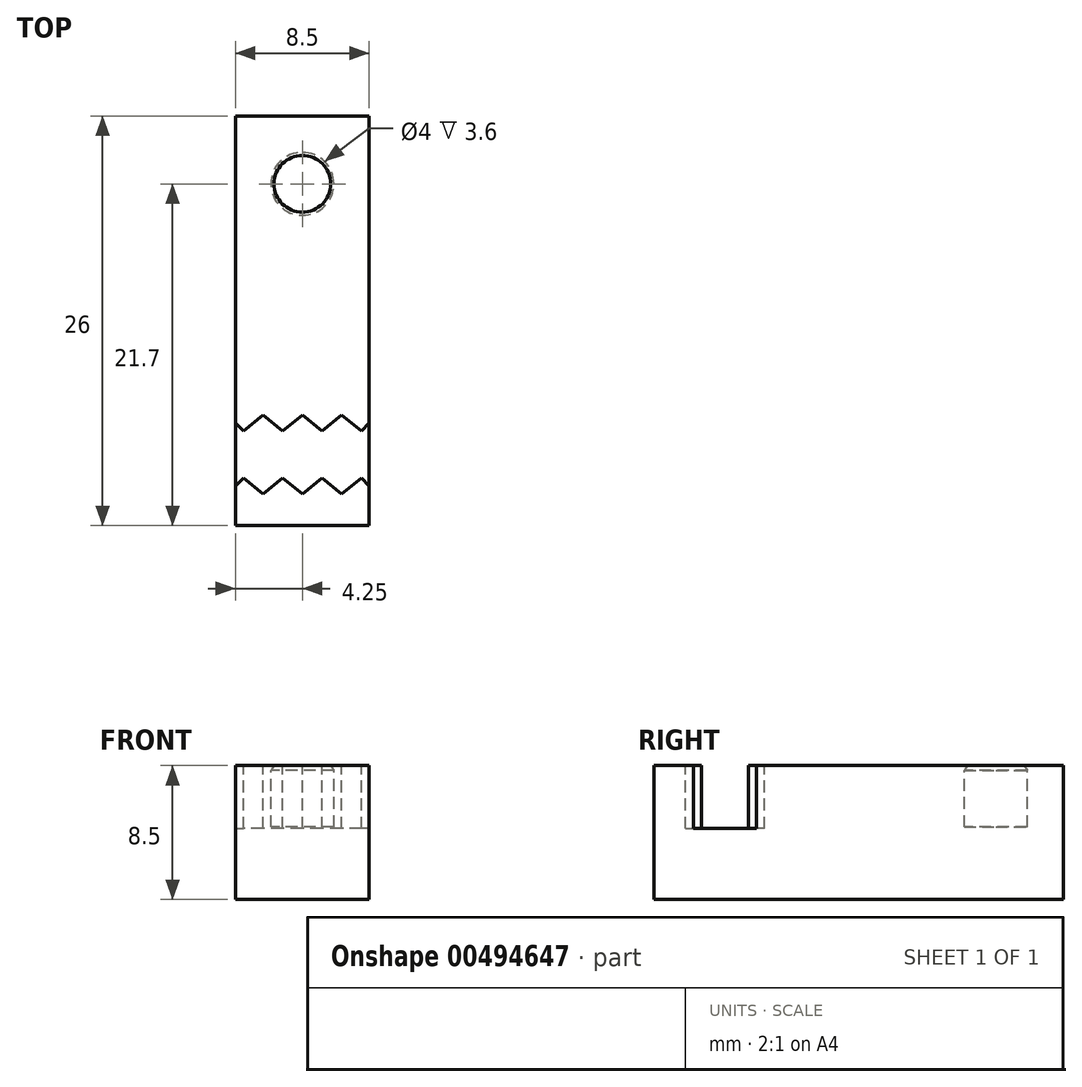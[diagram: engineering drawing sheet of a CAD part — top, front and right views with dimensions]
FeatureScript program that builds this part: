
annotation { "Feature Type Name" : "Feature", "Feature Type Description" : "" }
export const myFeature = defineFeature(function(context is Context, id is Id, definition is map)
    precondition{}
    {
        {
            var Q0;
            Q0=qCreatedBy(makeId("Top.planeOp"),FACE);
            var sketch = newSketch(context, id + "F0", { "sketchPlane" : qUnion([Q0])});
            skLineSegment(sketch, "E0.bottom", {"start": v(-4.25, 0) * mm, "end": v(4.25, 0) * mm});
            skLineSegment(sketch, "E0.top", {"start": v(-4.25, 26) * mm, "end": v(4.25, 26) * mm});
            skLineSegment(sketch, "E0.left", {"start": v(-4.25, 0) * mm, "end": v(-4.25, 26) * mm});
            skLineSegment(sketch, "E0.right", {"start": v(4.25, 0) * mm, "end": v(4.25, 26) * mm});
            skPoint(sketch, "E1", {"position": v(0, 0) * mm});
            skSolve(sketch);
        }
        {
            var Q0;
            Q0=makeQuery(id+"F0.imprint","IMPRINT",FACE,{"disambiguationData":[TD([[makeQuery(id+"F0.imprint","IMPRINT",EDGE,{"derivedFrom":sQuery(id+"F0.wireOp",EDGE,"E0.bottom")}),1.0]])]});
            extrude(context, id + "F1", {"entities" : qUnion([Q0]), "endBound" : BoundingType.SYMMETRIC, "depth" : 8.5 * mm});
        }
        {
            var Q0;
            Q0=qCreatedBy(makeId("Right.planeOp"),FACE);
            var sketch = newSketch(context, id + "F2", { "sketchPlane" : qUnion([Q0])});
            skLineSegment(sketch, "E2", {"start": v(23.5, 4.25) * mm, "end": v(23.7, 3.95) * mm});
            skLineSegment(sketch, "E3", {"start": v(23.7, 3.95) * mm, "end": v(23.7, 0.35) * mm});
            skLineSegment(sketch, "E4", {"start": v(23.7, 0.35) * mm, "end": v(21.7, 0.35) * mm});
            skLineSegment(sketch, "E5", {"start": v(21.7, 0.35) * mm, "end": v(21.7, 4.25) * mm});
            skLineSegment(sketch, "E6", {"start": v(21.7, 4.25) * mm, "end": v(23.5, 4.25) * mm});
            skSolve(sketch);
        }
        {
            var Q0;
            Q0 = qSketchRegion(id + "F2", true);
            var Q1;
            Q1=sQuery(id+"F2.wireOp",EDGE,"E5");
            revolve(context, id + "F3", {"operationType" : NewBodyOperationType.REMOVE, "entities" : qUnion([Q0]), "axis" : qUnion([Q1]), "revolveType" : RevolveType.FULL, "oppositeDirection" : true});
        }
        {
            var Q0;
            Q0=makeQuery(id+"F1.opExtrude","CAP_FACE",FACE,{"disambiguationData":[OSD([sQuery(id+"F0.wireOp",EDGE,"E0.bottom"),sQuery(id+"F0.wireOp",EDGE,"E0.top"),sQuery(id+"F0.wireOp",EDGE,"E0.left"),sQuery(id+"F0.wireOp",EDGE,"E0.right")])],"isStart":false});
            var sketch = newSketch(context, id + "F4", { "sketchPlane" : qUnion([Q0])});
            skLineSegment(sketch, "E7", {"start": v(-4.25, 6.5) * mm, "end": v(-3.75, 6) * mm});
            skLineSegment(sketch, "E8", {"start": v(-3.75, 6) * mm, "end": v(-2.5, 7) * mm});
            skLineSegment(sketch, "E9", {"start": v(-2.5, 7) * mm, "end": v(-1.25, 6) * mm});
            skLineSegment(sketch, "E10", {"start": v(-1.25, 6) * mm, "end": v(0, 7) * mm});
            skLineSegment(sketch, "E11", {"start": v(0, 7) * mm, "end": v(1.25, 6) * mm});
            skLineSegment(sketch, "E12", {"start": v(2.5, 7) * mm, "end": v(3.75, 6) * mm});
            skLineSegment(sketch, "E13", {"start": v(2.5, 7) * mm, "end": v(1.25, 6) * mm});
            skLineSegment(sketch, "E14", {"start": v(3.75, 6) * mm, "end": v(4.25, 6.5) * mm});
            skLineSegment(sketch, "E15", {"start": v(4.25, 6.5) * mm, "end": v(4.25, 2.5) * mm});
            skLineSegment(sketch, "E16", {"start": v(4.25, 2.5) * mm, "end": v(3.75, 3) * mm});
            skLineSegment(sketch, "E17", {"start": v(3.75, 3) * mm, "end": v(2.5, 2) * mm});
            skLineSegment(sketch, "E18", {"start": v(2.5, 2) * mm, "end": v(1.25, 3) * mm});
            skLineSegment(sketch, "E19", {"start": v(1.25, 3) * mm, "end": v(0, 2) * mm});
            skLineSegment(sketch, "E20", {"start": v(0, 2) * mm, "end": v(-1.25, 3) * mm});
            skLineSegment(sketch, "E21", {"start": v(-1.25, 3) * mm, "end": v(-2.5, 2) * mm});
            skLineSegment(sketch, "E22", {"start": v(-2.5, 2) * mm, "end": v(-3.75, 3) * mm});
            skLineSegment(sketch, "E23", {"start": v(-3.75, 3) * mm, "end": v(-4.25, 2.5) * mm});
            skLineSegment(sketch, "E24", {"start": v(-4.25, 2.5) * mm, "end": v(-4.25, 6.5) * mm});
            skSolve(sketch);
        }
        {
            var Q0;
            Q0=makeQuery(id+"F4.imprint","IMPRINT",FACE,{"disambiguationData":[TD([[makeQuery(id+"F4.imprint","IMPRINT",EDGE,{"derivedFrom":sQuery(id+"F4.wireOp",EDGE,"E7")}),-1.0]])]});
            extrude(context, id + "F5", {"entities" : qUnion([Q0]), "operationType" : NewBodyOperationType.REMOVE, "oppositeDirection" : true, "depth" : 4 * mm});
        }
    });
